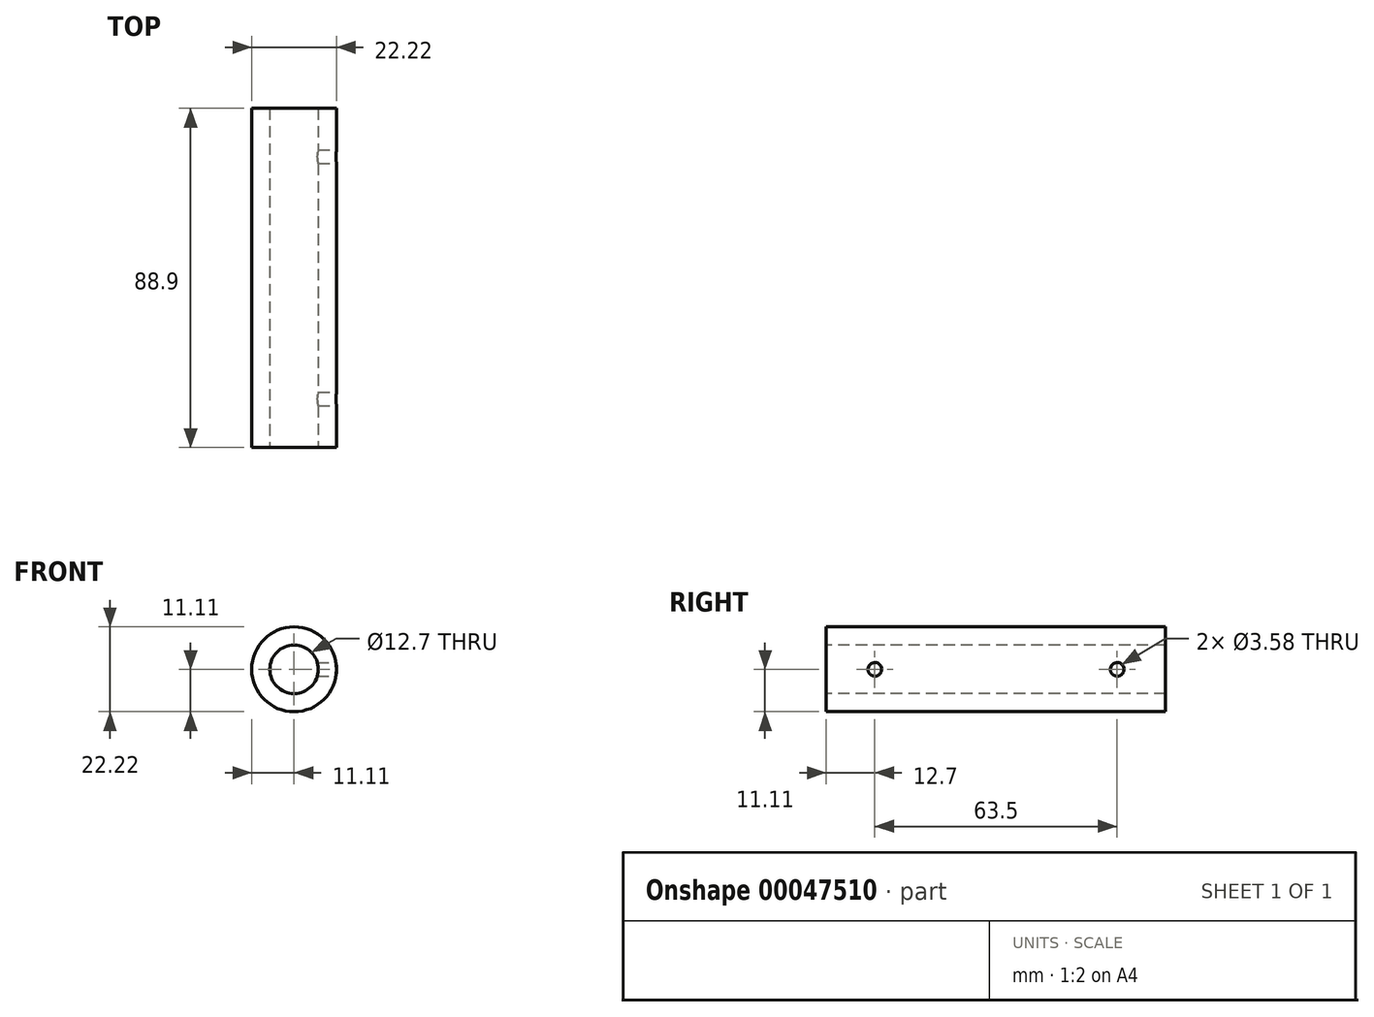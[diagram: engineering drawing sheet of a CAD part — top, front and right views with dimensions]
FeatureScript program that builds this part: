
annotation { "Feature Type Name" : "Feature", "Feature Type Description" : "" }
export const myFeature = defineFeature(function(context is Context, id is Id, definition is map)
    precondition{}
    {
        {
            var Q0;
            Q0=qCreatedBy(makeId("Front.planeOp"),FACE);
            var sketch = newSketch(context, id + "F0", { "sketchPlane" : qUnion([Q0])});
            skLineSegment(sketch, "E0.rect.bottom", {"start": v(-11.11, 11.11) * mm, "end": v(11.11, 11.11) * mm});
            skLineSegment(sketch, "E0.rect.top", {"start": v(-11.11, -11.11) * mm, "end": v(11.11, -11.11) * mm});
            skLineSegment(sketch, "E0.rect.left", {"start": v(-11.11, 11.11) * mm, "end": v(-11.11, -11.11) * mm});
            skLineSegment(sketch, "E0.rect.right", {"start": v(11.11, 11.11) * mm, "end": v(11.11, -11.11) * mm});
            skPoint(sketch, "E0.rect.middle", {"position": v(0, 0) * mm});
            skSolve(sketch);
        }
        {
            var Q0;
            Q0=makeQuery(id+"F0.imprint","IMPRINT",FACE,{"disambiguationData":[TD([[makeQuery(id+"F0.imprint","IMPRINT",EDGE,{"derivedFrom":sQuery(id+"F0.wireOp",EDGE,"E0.rect.bottom")}),-1.0]])]});
            extrude(context, id + "F1", {"entities" : qUnion([Q0]), "endBound" : BoundingType.SYMMETRIC, "depth" : 88.9 * mm});
        }
        {
            var Q0;
            Q0=makeQuery(id+"F1.opExtrude","SWEPT_FACE",FACE,{"disambiguationData":[OSD([sQuery(id+"F0.wireOp",EDGE,"E0.rect.right")])]});
            var sketch = newSketch(context, id + "F2", { "sketchPlane" : qUnion([Q0])});
            skCircle(sketch, "E1", {"center": v(31.75, 0) * mm, "radius": 1.8 * mm});
            skSolve(sketch);
        }
        {
            var Q0;
            Q0=makeQuery(id+"F2.imprint","IMPRINT",FACE,{"disambiguationData":[TD([[makeQuery(id+"F2.imprint","IMPRINT",EDGE,{"derivedFrom":sQuery(id+"F2.wireOp",EDGE,"E1")}),1.0]])]});
            extrude(context, id + "F3", {"entities" : qUnion([Q0]), "operationType" : NewBodyOperationType.REMOVE, "oppositeDirection" : true, "depth" : 10.16 * mm});
        }
        {
            var Q0;
            Q0=makeQuery(id+"F1.opExtrude","SWEPT_FACE",FACE,{"disambiguationData":[OSD([sQuery(id+"F0.wireOp",EDGE,"E0.rect.right")])]});
            var sketch = newSketch(context, id + "F4", { "sketchPlane" : qUnion([Q0])});
            skCircle(sketch, "E2", {"center": v(-31.75, 0) * mm, "radius": 1.8 * mm});
            skSolve(sketch);
        }
        {
            var Q0;
            Q0=makeQuery(id+"F4.imprint","IMPRINT",FACE,{"disambiguationData":[TD([[makeQuery(id+"F4.imprint","IMPRINT",EDGE,{"derivedFrom":sQuery(id+"F4.wireOp",EDGE,"E2")}),1.0]])]});
            extrude(context, id + "F5", {"entities" : qUnion([Q0]), "operationType" : NewBodyOperationType.REMOVE, "oppositeDirection" : true, "depth" : 10.16 * mm});
        }
        {
            var Q0;
            Q0=makeQuery(id+"F1.opExtrude","CAP_FACE",FACE,{"disambiguationData":[OSD([sQuery(id+"F0.wireOp",EDGE,"E0.rect.bottom"),sQuery(id+"F0.wireOp",EDGE,"E0.rect.top"),sQuery(id+"F0.wireOp",EDGE,"E0.rect.left"),sQuery(id+"F0.wireOp",EDGE,"E0.rect.right")])],"isStart":false});
            var sketch = newSketch(context, id + "F6", { "sketchPlane" : qUnion([Q0])});
            skCircle(sketch, "E3", {"center": v(0, 0) * mm, "radius": 11.11 * mm});
            skLineSegment(sketch, "E4", {"start": v(-11.11, 11.11) * mm, "end": v(-11.11, -11.11) * mm});
            skLineSegment(sketch, "E5", {"start": v(-11.11, -11.11) * mm, "end": v(11.11, -11.11) * mm});
            skLineSegment(sketch, "E6", {"start": v(11.11, -11.11) * mm, "end": v(11.11, 11.11) * mm});
            skLineSegment(sketch, "E7", {"start": v(-11.11, 11.11) * mm, "end": v(-9.53, 11.11) * mm});
            skLineSegment(sketch, "E8", {"start": v(11.11, 11.11) * mm, "end": v(-11.11, 11.11) * mm});
            skSolve(sketch);
        }
        {
            var Q0;
            {var subQ0=sQuery(id+"F6.wireOp",EDGE,"E8");var subQ1=sQuery(id+"F6.wireOp",EDGE,"E3");var subQ2=makeQuery(id+"F6.imprint","INTERSECT",VERTEX,{"derivedFrom":[subQ1,subQ0]});Q0=makeQuery(id+"F6.imprint","IMPRINT",FACE,{"disambiguationData":[TD([[makeQuery(id+"F6.imprint","IMPRINT",EDGE,{"disambiguationData":[TD([[subQ2,-1.0]])],"derivedFrom":subQ1}),-1.0]])]});}
            var Q1;
            {var subQ0=sQuery(id+"F6.wireOp",EDGE,"E8");var subQ1=sQuery(id+"F6.wireOp",EDGE,"E3");var subQ2=makeQuery(id+"F6.imprint","INTERSECT",VERTEX,{"derivedFrom":[subQ1,subQ0]});Q1=makeQuery(id+"F6.imprint","IMPRINT",FACE,{"disambiguationData":[TD([[makeQuery(id+"F6.imprint","IMPRINT",EDGE,{"disambiguationData":[TD([[subQ2,1.0]])],"derivedFrom":subQ1}),-1.0]])]});}
            var Q2;
            {var subQ0=sQuery(id+"F6.wireOp",EDGE,"E6");var subQ1=sQuery(id+"F6.wireOp",EDGE,"E3");var subQ2=makeQuery(id+"F6.imprint","INTERSECT",VERTEX,{"derivedFrom":[subQ1,subQ0]});Q2=makeQuery(id+"F6.imprint","IMPRINT",FACE,{"disambiguationData":[TD([[makeQuery(id+"F6.imprint","IMPRINT",EDGE,{"disambiguationData":[TD([[subQ2,1.0]])],"derivedFrom":subQ1}),-1.0]])]});}
            var Q3;
            {var subQ0=sQuery(id+"F6.wireOp",EDGE,"E4");var subQ1=sQuery(id+"F6.wireOp",EDGE,"E3");var subQ2=makeQuery(id+"F6.imprint","INTERSECT",VERTEX,{"derivedFrom":[subQ1,subQ0]});Q3=makeQuery(id+"F6.imprint","IMPRINT",FACE,{"disambiguationData":[TD([[makeQuery(id+"F6.imprint","IMPRINT",EDGE,{"disambiguationData":[TD([[subQ2,-1.0]])],"derivedFrom":subQ1}),-1.0]])]});}
            extrude(context, id + "F7", {"entities" : qUnion([Q0, Q1, Q2, Q3]), "operationType" : NewBodyOperationType.REMOVE, "oppositeDirection" : true, "depth" : 88.9 * mm});
        }
        {
            var Q0;
            Q0=makeQuery(id+"F1.opExtrude","CAP_FACE",FACE,{"disambiguationData":[OSD([sQuery(id+"F0.wireOp",EDGE,"E0.rect.bottom"),sQuery(id+"F0.wireOp",EDGE,"E0.rect.top"),sQuery(id+"F0.wireOp",EDGE,"E0.rect.left"),sQuery(id+"F0.wireOp",EDGE,"E0.rect.right")])],"isStart":false});
            var sketch = newSketch(context, id + "F8", { "sketchPlane" : qUnion([Q0])});
            skCircle(sketch, "E9", {"center": v(0, 0) * mm, "radius": 6.35 * mm});
            skSolve(sketch);
        }
        {
            var Q0;
            Q0=makeQuery(id+"F8.imprint","IMPRINT",FACE,{"disambiguationData":[TD([[makeQuery(id+"F8.imprint","IMPRINT",EDGE,{"derivedFrom":sQuery(id+"F8.wireOp",EDGE,"E9")}),1.0]])]});
            extrude(context, id + "F9", {"entities" : qUnion([Q0]), "operationType" : NewBodyOperationType.REMOVE, "oppositeDirection" : true, "depth" : 88.9 * mm});
        }
    });
